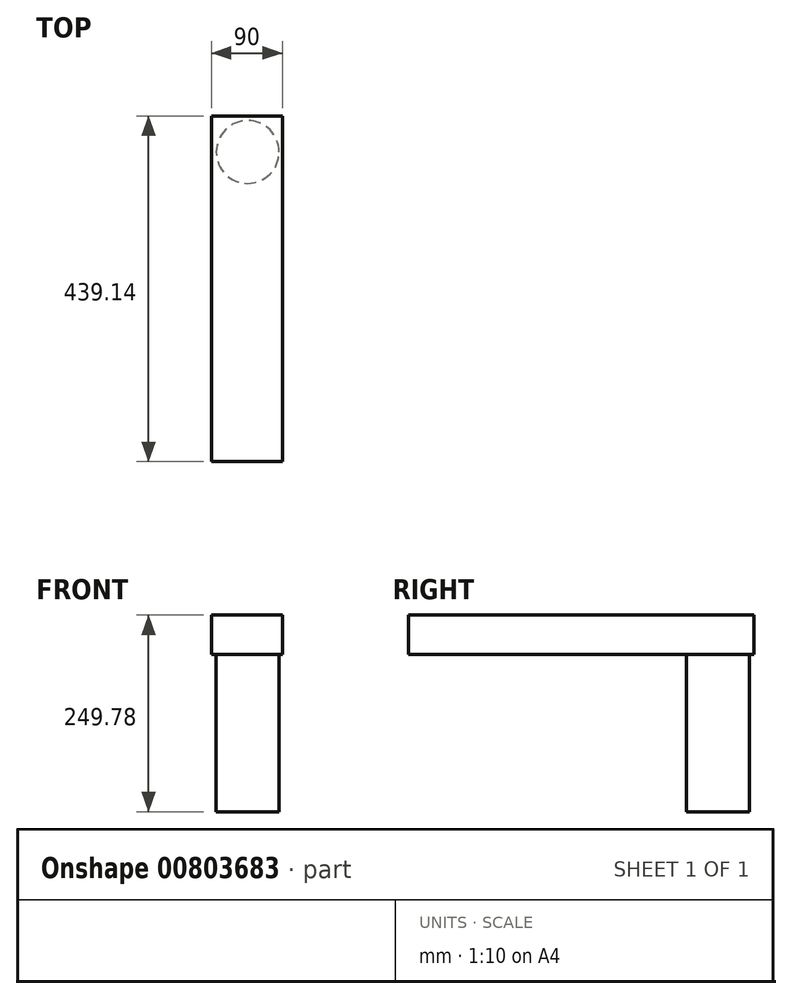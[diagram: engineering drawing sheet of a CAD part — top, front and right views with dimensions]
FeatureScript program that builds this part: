
annotation { "Feature Type Name" : "Feature", "Feature Type Description" : "" }
export const myFeature = defineFeature(function(context is Context, id is Id, definition is map)
    precondition{}
    {
        {
            var Q0;
            Q0=qCreatedBy(makeId("Right.planeOp"),FACE);
            var sketch = newSketch(context, id + "F0", { "sketchPlane" : qUnion([Q0])});
            skLineSegment(sketch, "E0.bottom", {"start": v(0, 0) * mm, "end": v(-439.14, 0) * mm});
            skLineSegment(sketch, "E0.top", {"start": v(0, 49.78) * mm, "end": v(-439.14, 49.78) * mm});
            skLineSegment(sketch, "E0.left", {"start": v(0, 0) * mm, "end": v(0, 49.78) * mm});
            skLineSegment(sketch, "E0.right", {"start": v(-439.14, 0) * mm, "end": v(-439.14, 49.78) * mm});
            skSolve(sketch);
        }
        {
            var Q0;
            Q0 = qSketchRegion(id + "F0", true);
            extrude(context, id + "F1", {"entities" : qUnion([Q0]), "depth" : 90 * mm, "offsetDistance" : 25 * mm});
        }
        {
            var Q0;
            Q0=makeQuery(id+"F1.opExtrude","SWEPT_FACE",FACE,{"disambiguationData":[OSD([sQuery(id+"F0.wireOp",EDGE,"E0.bottom")])]});
            var sketch = newSketch(context, id + "F2", { "sketchPlane" : qUnion([Q0])});
            skSolve(sketch);
        }
        {
            var Q0;
            {var subQ0=sQuery(id+"F0.wireOp",EDGE,"E0.bottom");Q0=makeQuery(id+"F2.imprint","IMPRINT",FACE,{"disambiguationData":[TD([[makeQuery(id+"F2.imprint","IMPRINT",EDGE,{"derivedFrom":makeQuery(id+"F1.opExtrude","CAP_EDGE",EDGE,{"disambiguationData":[OSD([subQ0])],"isStart":true})}),-1.0]])]});}
            var sketch = newSketch(context, id + "F3", { "sketchPlane" : qUnion([Q0])});
            skCircle(sketch, "E1", {"center": v(46.05, 45.84) * mm, "radius": 39.93 * mm});
            skSolve(sketch);
        }
        {
            var Q0;
            Q0 = qSketchRegion(id + "F3", true);
            extrude(context, id + "F4", {"entities" : qUnion([Q0]), "operationType" : NewBodyOperationType.ADD, "depth" : 200 * mm, "offsetDistance" : 25 * mm});
        }
    });
